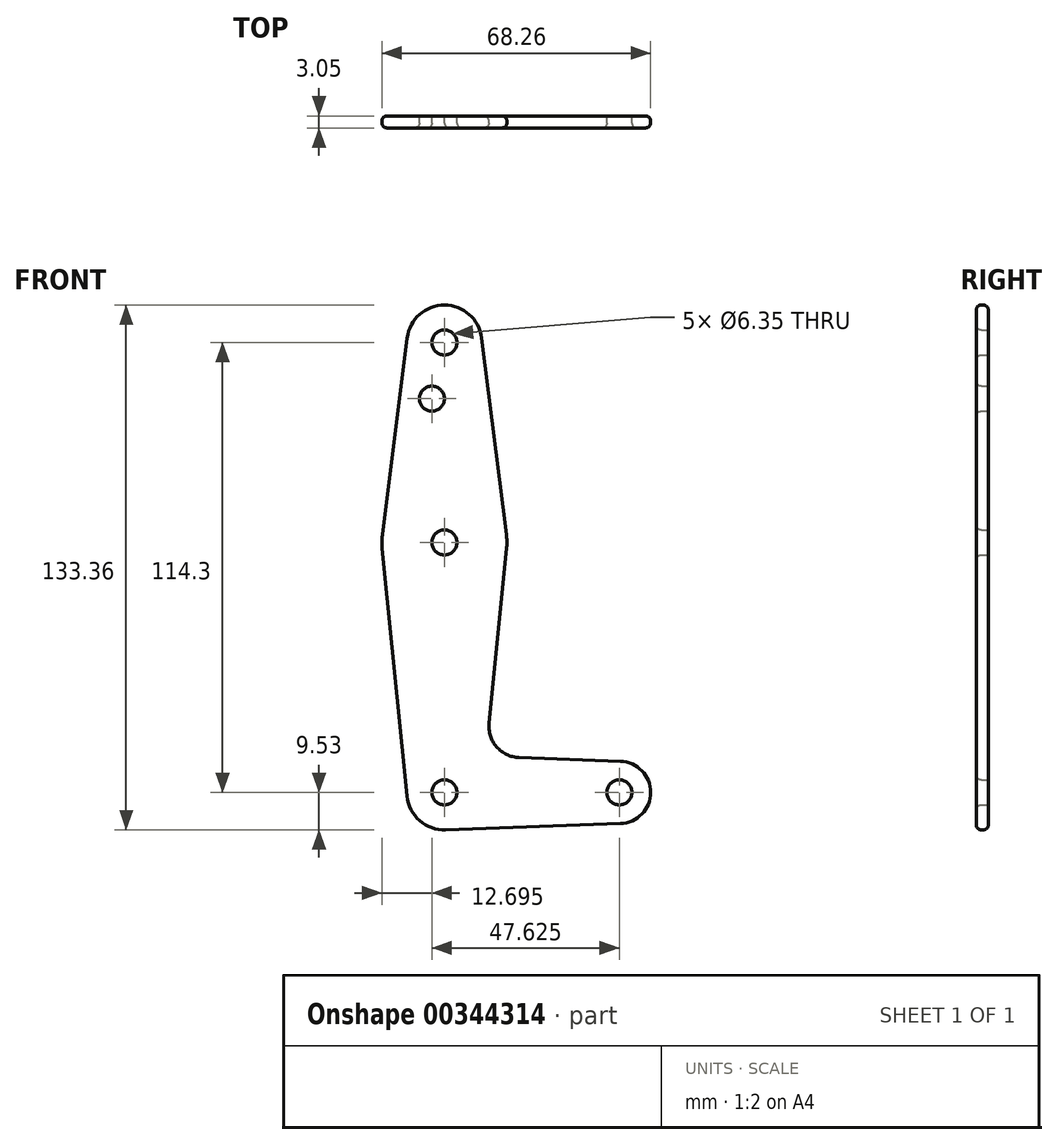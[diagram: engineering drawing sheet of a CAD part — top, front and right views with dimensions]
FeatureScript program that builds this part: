
annotation { "Feature Type Name" : "Feature", "Feature Type Description" : "" }
export const myFeature = defineFeature(function(context is Context, id is Id, definition is map)
    precondition{}
    {
        {
            var Q0;
            Q0=qCreatedBy(makeId("Front.planeOp"),FACE);
            var sketch = newSketch(context, id + "F0", { "sketchPlane" : qUnion([Q0])});
            skLineSegment(sketch, "E0", {"start": v(0, 0) * mm, "end": v(0, 114.3) * mm, "construction": true});
            skLineSegment(sketch, "E1", {"start": v(0, 0) * mm, "end": v(44.45, 0) * mm, "construction": true});
            skCircle(sketch, "E2", {"center": v(44.45, 0) * mm, "radius": 7.94 * mm});
            skCircle(sketch, "E3", {"center": v(0, 0) * mm, "radius": 9.53 * mm});
            skCircle(sketch, "E4", {"center": v(0, 114.3) * mm, "radius": 9.53 * mm});
            skCircle(sketch, "E5", {"center": v(0, 63.5) * mm, "radius": 15.88 * mm});
            skLineSegment(sketch, "E6", {"start": v(-15.75, 65.48) * mm, "end": v(-9.45, 115.5) * mm});
            skLineSegment(sketch, "E7", {"start": v(15.8, 61.91) * mm, "end": v(11.34, 17.6) * mm});
            skLineSegment(sketch, "E8", {"start": v(-9.48, -0.95) * mm, "end": v(-15.8, 61.91) * mm});
            skLineSegment(sketch, "E9", {"start": v(44.73, -7.93) * mm, "end": v(0.34, -9.52) * mm});
            skLineSegment(sketch, "E10", {"start": v(9.45, 115.5) * mm, "end": v(15.75, 65.48) * mm});
            skLineSegment(sketch, "E11", {"start": v(44.73, 7.93) * mm, "end": v(18.97, 8.85) * mm});
            skCircle(sketch, "E12", {"center": v(0, 114.3) * mm, "radius": 3.18 * mm});
            skCircle(sketch, "E13", {"center": v(0, 63.5) * mm, "radius": 3.18 * mm});
            skCircle(sketch, "E14", {"center": v(0, 0) * mm, "radius": 3.18 * mm});
            skCircle(sketch, "E15", {"center": v(44.45, 0) * mm, "radius": 3.18 * mm});
            skCircle(sketch, "E16", {"center": v(-3.18, 100.03) * mm, "radius": 3.18 * mm});
            skPoint(sketch, "E17.newPointB", {"position": v(0, 9.53) * mm});
            skArc(sketch, "E17.filletArc", {"start": v(11.34, 17.6) * mm, "mid": v(13.26, 11.57) * mm, "end": v(18.97, 8.85) * mm});
            skSolve(sketch);
        }
        {
            var Q0;
            Q0 = qSketchRegion(id + "F0", true);
            extrude(context, id + "F1", {"entities" : qUnion([Q0]), "depth" : 3.05 * mm});
        }
        {
            var Q0;
            Q0=makeQuery(id+"F1.opExtrude","CAP_EDGE",EDGE,{"disambiguationData":[OSD([sQuery(id+"F0.wireOp",EDGE,"E8")])],"isStart":true});
            fillet(context, id + "F2", {"entities" : qUnion([Q0]), "radius" : 1.27 * mm, "tangentPropagation" : true, "allowEdgeOverflow" : false});
        }
        {
            var Q0;
            {var subQ0=sQuery(id+"F0.wireOp",EDGE,"E8");Q0=makeQuery(id+"F2.opFillet","BLEND_EDGE",EDGE,{"blendedFrom":[makeQuery(id+"F1.opExtrude","CAP_EDGE",EDGE,{"disambiguationData":[OSD([subQ0])],"isStart":true}),makeQuery(id+"F1.opExtrude","CAP_FACE",FACE,{"disambiguationData":[OSD([sQuery(id+"F0.wireOp",EDGE,"E2"),sQuery(id+"F0.wireOp",EDGE,"E3"),sQuery(id+"F0.wireOp",EDGE,"E4"),sQuery(id+"F0.wireOp",EDGE,"E5"),sQuery(id+"F0.wireOp",EDGE,"E6"),sQuery(id+"F0.wireOp",EDGE,"E7"),subQ0,sQuery(id+"F0.wireOp",EDGE,"E9"),sQuery(id+"F0.wireOp",EDGE,"E10"),sQuery(id+"F0.wireOp",EDGE,"E11"),sQuery(id+"F0.wireOp",EDGE,"E12"),sQuery(id+"F0.wireOp",EDGE,"E13"),sQuery(id+"F0.wireOp",EDGE,"E14"),sQuery(id+"F0.wireOp",EDGE,"E15"),sQuery(id+"F0.wireOp",EDGE,"E16"),sQuery(id+"F0.wireOp",EDGE,"E17.filletArc")])],"isStart":false})],"blendedInto":[makeQuery(id+"F1.opExtrude","CAP_FACE",FACE,{"disambiguationData":[OSD([sQuery(id+"F0.wireOp",EDGE,"E2"),sQuery(id+"F0.wireOp",EDGE,"E3"),sQuery(id+"F0.wireOp",EDGE,"E4"),sQuery(id+"F0.wireOp",EDGE,"E5"),sQuery(id+"F0.wireOp",EDGE,"E6"),sQuery(id+"F0.wireOp",EDGE,"E7"),subQ0,sQuery(id+"F0.wireOp",EDGE,"E9"),sQuery(id+"F0.wireOp",EDGE,"E10"),sQuery(id+"F0.wireOp",EDGE,"E11"),sQuery(id+"F0.wireOp",EDGE,"E12"),sQuery(id+"F0.wireOp",EDGE,"E13"),sQuery(id+"F0.wireOp",EDGE,"E14"),sQuery(id+"F0.wireOp",EDGE,"E15"),sQuery(id+"F0.wireOp",EDGE,"E16"),sQuery(id+"F0.wireOp",EDGE,"E17.filletArc")])],"isStart":false})]});}
            var Q1;
            Q1=makeQuery(id+"F1.opExtrude","CAP_FACE",FACE,{"disambiguationData":[OSD([sQuery(id+"F0.wireOp",EDGE,"E2"),sQuery(id+"F0.wireOp",EDGE,"E3"),sQuery(id+"F0.wireOp",EDGE,"E4"),sQuery(id+"F0.wireOp",EDGE,"E5"),sQuery(id+"F0.wireOp",EDGE,"E6"),sQuery(id+"F0.wireOp",EDGE,"E7"),sQuery(id+"F0.wireOp",EDGE,"E8"),sQuery(id+"F0.wireOp",EDGE,"E9"),sQuery(id+"F0.wireOp",EDGE,"E10"),sQuery(id+"F0.wireOp",EDGE,"E11"),sQuery(id+"F0.wireOp",EDGE,"E12"),sQuery(id+"F0.wireOp",EDGE,"E13"),sQuery(id+"F0.wireOp",EDGE,"E14"),sQuery(id+"F0.wireOp",EDGE,"E15"),sQuery(id+"F0.wireOp",EDGE,"E16"),sQuery(id+"F0.wireOp",EDGE,"E17.filletArc")])],"isStart":false});
            fillet(context, id + "F3", {"entities" : qUnion([Q0, Q1]), "radius" : 1.27 * mm, "tangentPropagation" : true, "allowEdgeOverflow" : false});
        }
    });
